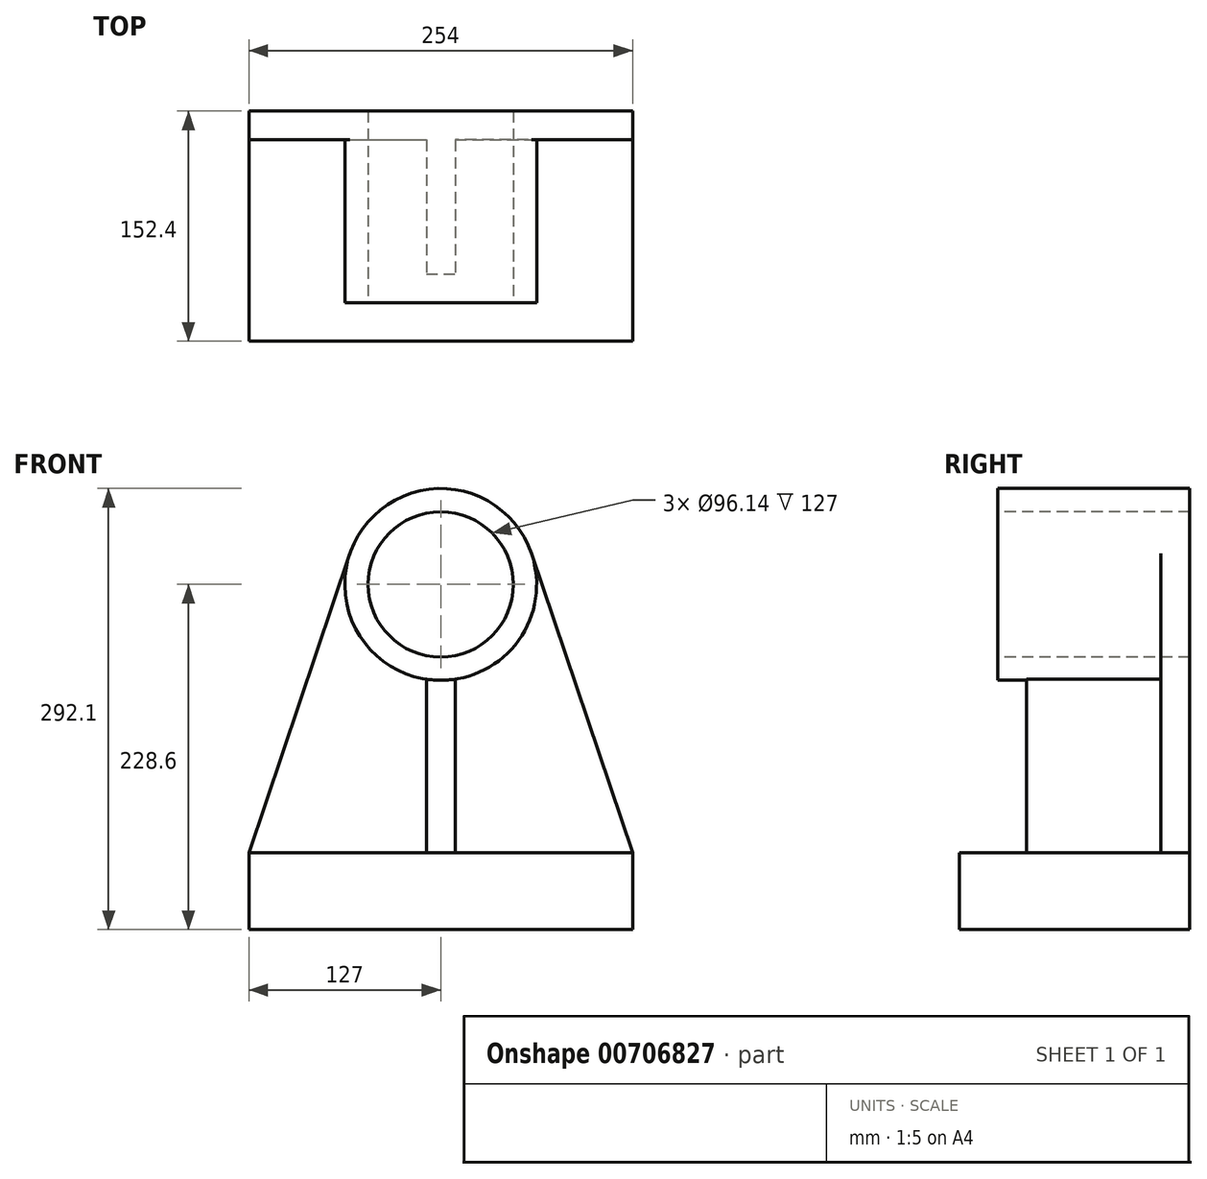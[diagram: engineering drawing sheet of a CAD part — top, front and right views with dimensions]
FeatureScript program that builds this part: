
annotation { "Feature Type Name" : "Feature", "Feature Type Description" : "" }
export const myFeature = defineFeature(function(context is Context, id is Id, definition is map)
    precondition{}
    {
        {
            var Q0;
            Q0=qCreatedBy(makeId("Front.planeOp"),FACE);
            var sketch = newSketch(context, id + "F0", { "sketchPlane" : qUnion([Q0])});
            skLineSegment(sketch, "E0.bottom", {"start": v(127, -25.4) * mm, "end": v(-127, -25.4) * mm});
            skLineSegment(sketch, "E0.left", {"start": v(127, -25.4) * mm, "end": v(127, 25.4) * mm});
            skLineSegment(sketch, "E0.right", {"start": v(-127, -25.4) * mm, "end": v(-127, 25.4) * mm});
            skPoint(sketch, "E0.middle", {"position": v(0, 0) * mm});
            skArc(sketch, "E1", {"start": v(60.17, 223.5) * mm, "mid": v(0, 266.7) * mm, "end": v(-60.17, 223.5) * mm});
            skLineSegment(sketch, "E2", {"start": v(-127, 25.4) * mm, "end": v(-60.17, 223.5) * mm});
            skLineSegment(sketch, "E3", {"start": v(127, 25.4) * mm, "end": v(60.17, 223.5) * mm});
            skSolve(sketch);
        }
        {
            var Q0;
            Q0=qSketchRegion(id+"F0",true);
            extrude(context, id + "F1", {"entities" : qUnion([Q0]), "depth" : 152.4 * mm, "offsetDistance" : 25.4 * mm});
        }
        {
            var Q0;
            Q0=makeQuery(id+"F1.opExtrude","CAP_FACE",FACE,{"disambiguationData":[OSD([sQuery(id+"F0.wireOp",EDGE,"E0.bottom"),sQuery(id+"F0.wireOp",EDGE,"E0.left"),sQuery(id+"F0.wireOp",EDGE,"E0.right"),sQuery(id+"F0.wireOp",EDGE,"E1"),sQuery(id+"F0.wireOp",EDGE,"E2"),sQuery(id+"F0.wireOp",EDGE,"E3")])],"isStart":false});
            var sketch = newSketch(context, id + "F2", { "sketchPlane" : qUnion([Q0])});
            skArc(sketch, "E4", {"start": v(-60.17, 223.5) * mm, "mid": v(-54.22, 170.15) * mm, "end": v(-9.53, 140.42) * mm});
            skLineSegment(sketch, "E5", {"start": v(-127, 25.4) * mm, "end": v(-9.53, 25.4) * mm});
            skLineSegment(sketch, "E6", {"start": v(-127, 25.4) * mm, "end": v(-60.17, 223.5) * mm});
            skLineSegment(sketch, "E7", {"start": v(-9.53, 25.4) * mm, "end": v(-9.53, 140.42) * mm});
            skLineSegment(sketch, "E8", {"start": v(127, 25.4) * mm, "end": v(9.52, 25.4) * mm});
            skLineSegment(sketch, "E9", {"start": v(9.52, 25.4) * mm, "end": v(9.52, 140.42) * mm});
            skLineSegment(sketch, "E10", {"start": v(127, 25.4) * mm, "end": v(60.17, 223.5) * mm});
            skArc(sketch, "E11.trimOffspring", {"start": v(9.52, 140.42) * mm, "mid": v(54.22, 170.15) * mm, "end": v(60.17, 223.5) * mm});
            skSolve(sketch);
        }
        {
            var Q0;
            Q0=qSketchRegion(id+"F2",true);
            extrude(context, id + "F3", {"entities" : qUnion([Q0]), "operationType" : NewBodyOperationType.REMOVE, "oppositeDirection" : true, "depth" : 133.35 * mm, "offsetDistance" : 25.4 * mm});
        }
        {
            var Q0;
            Q0=makeQuery(id+"F1.opExtrude","CAP_FACE",FACE,{"disambiguationData":[OSD([sQuery(id+"F0.wireOp",EDGE,"E0.bottom"),sQuery(id+"F0.wireOp",EDGE,"E0.left"),sQuery(id+"F0.wireOp",EDGE,"E0.right"),sQuery(id+"F0.wireOp",EDGE,"E1"),sQuery(id+"F0.wireOp",EDGE,"E2"),sQuery(id+"F0.wireOp",EDGE,"E3")])],"isStart":false});
            var sketch = newSketch(context, id + "F4", { "sketchPlane" : qUnion([Q0])});
            skCircle(sketch, "E12", {"center": v(0, 203.2) * mm, "radius": 48.07 * mm});
            skSolve(sketch);
        }
        {
            var Q0;
            Q0=qSketchRegion(id+"F4",true);
            extrude(context, id + "F5", {"entities" : qUnion([Q0]), "operationType" : NewBodyOperationType.REMOVE, "oppositeDirection" : true, "depth" : 152.4 * mm, "offsetDistance" : 25.4 * mm});
        }
        {
            var Q0;
            Q0=makeQuery(id+"F1.opExtrude","CAP_FACE",FACE,{"disambiguationData":[OSD([sQuery(id+"F0.wireOp",EDGE,"E0.bottom"),sQuery(id+"F0.wireOp",EDGE,"E0.left"),sQuery(id+"F0.wireOp",EDGE,"E0.right"),sQuery(id+"F0.wireOp",EDGE,"E1"),sQuery(id+"F0.wireOp",EDGE,"E2"),sQuery(id+"F0.wireOp",EDGE,"E3")])],"isStart":false});
            var sketch = newSketch(context, id + "F6", { "sketchPlane" : qUnion([Q0])});
            skLineSegment(sketch, "E13.bottom", {"start": v(-127, 25.4) * mm, "end": v(127, 25.4) * mm});
            skLineSegment(sketch, "E13.top", {"start": v(-127, 25.4) * mm, "end": v(127, 25.4) * mm});
            skLineSegment(sketch, "E13.left", {"start": v(-127, 25.4) * mm, "end": v(-127, 25.4) * mm});
            skLineSegment(sketch, "E13.right", {"start": v(127, 25.4) * mm, "end": v(127, 25.4) * mm});
            skLineSegment(sketch, "E14.bottom", {"start": v(-127, 25.4) * mm, "end": v(177.8, 25.4) * mm});
            skLineSegment(sketch, "E14.top", {"start": v(-127, 341.26) * mm, "end": v(177.8, 341.26) * mm});
            skLineSegment(sketch, "E14.left", {"start": v(-127, 25.4) * mm, "end": v(-127, 341.26) * mm});
            skLineSegment(sketch, "E14.right", {"start": v(177.8, 25.4) * mm, "end": v(177.8, 341.26) * mm});
            skSolve(sketch);
        }
        {
            var Q0;
            Q0=qSketchRegion(id+"F6",true);
            extrude(context, id + "F7", {"entities" : qUnion([Q0]), "operationType" : NewBodyOperationType.REMOVE, "oppositeDirection" : true, "depth" : 25.4 * mm, "offsetDistance" : 25.4 * mm});
        }
        {
            var Q0;
            Q0=makeQuery(id+"F7.boolean.opBoolean","COPY",FACE,{"derivedFrom":makeQuery(id+"F7.opExtrude","CAP_FACE",FACE,{"disambiguationData":[OSD([sQuery(id+"F6.wireOp",EDGE,"E14.bottom"),sQuery(id+"F6.wireOp",EDGE,"E14.top"),sQuery(id+"F6.wireOp",EDGE,"E14.left"),sQuery(id+"F6.wireOp",EDGE,"E14.right")])],"isStart":false})});
            var sketch = newSketch(context, id + "F8", { "sketchPlane" : qUnion([Q0])});
            skArc(sketch, "E15", {"start": v(-9.53, 140.42) * mm, "mid": v(0, 139.7) * mm, "end": v(9.52, 140.42) * mm});
            skLineSegment(sketch, "E16", {"start": v(-9.53, 140.42) * mm, "end": v(-9.53, 25.4) * mm});
            skLineSegment(sketch, "E17", {"start": v(-9.53, 25.4) * mm, "end": v(9.52, 25.4) * mm});
            skLineSegment(sketch, "E18", {"start": v(9.52, 25.4) * mm, "end": v(9.52, 140.42) * mm});
            skSolve(sketch);
        }
        {
            var Q0;
            Q0=qSketchRegion(id+"F8",true);
            extrude(context, id + "F9", {"entities" : qUnion([Q0]), "operationType" : NewBodyOperationType.REMOVE, "oppositeDirection" : true, "depth" : 19.05 * mm, "offsetDistance" : 25.4 * mm});
        }
    });
